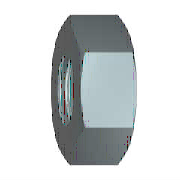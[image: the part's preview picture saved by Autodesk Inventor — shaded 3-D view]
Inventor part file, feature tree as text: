
AUTODESK INVENTOR PART (.ipt)
format: ipt  version: 2020 (Build 240168000, 168)  size: 163,840 bytes
history: native  units: mm (DEFAULTED — no unit token found)
features: sketch x3, chamfer x1, hole x1, other x1, plane x1
ambient origin geometry x7: Origin, YZ Plane, XZ Plane, X Axis, Y Axis, Z Axis, Center Point
bodies: Solid1 (feature_tree), Body (feature_tree)
feature tree (7):
  chamfer  "Chamfer1"  Angle=30.0deg  [1 undecoded]
  hole  "Thread"  [1 undecoded]
  other  "Work Axis1"
  plane  "Work Plane1"
  sketch  "Sketch1"  dims[d0=8.082904mm]
  sketch  "Sketch2"  dims[d1=3.2mm]
  sketch  "Sketch3"  dims[d2=0.0mm d3=30.0deg d4=30.0deg d5=5.9mm d6=5.9mm d7=90.0deg d25=3.242mm d26=6.0mm d27=4.0mm d28=2.0mm d29=14.3117mm d30=8.0mm d31=20.594885mm d8=0.378886mm d9=30.0deg d10=0.378886mm d11=30.0deg d13=0.0mm d14=0.0mm d39=0.0mm d40=0.378886mm d41=0.378886mm d42=0.0mm]
note: 2 required parameter values undecoded (feature->parameter linkage not recoverable at this tier; creation-order binding heuristic only, values carry confidence <= 0.55)
